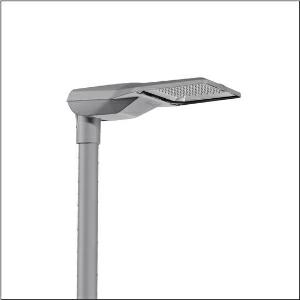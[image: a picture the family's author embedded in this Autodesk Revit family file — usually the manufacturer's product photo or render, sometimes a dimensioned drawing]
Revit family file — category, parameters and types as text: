
# Revit family: streetlight_sl_21_iq_midi___pc-r_5xe3g31g08mb_83c1
name_source: partatom
category: Lighting Fixtures
units: mm (PartAtom-declared; Revit-internal decimal feet)

## family parameters
Cut with Voids When Loaded = No
Host = Face
Light Source = No
Part Type = Normal
Room Calculation Point = No
Round Connector Dimension = Use Diameter
Shared = No

## types (1)
- --- (1 x LED, 18560 lm, 146.7 W, 3000K)
    Apparent Load = 147 VA
    CIE Flux Codes = 38 78 98 100 100
    Color Rendering = 70
    Color Temperature = 3000K
    Default Elevation = 1800 mm
    Description = Streetlight SL 21 iQ midi, mast luminaire, primary light control with lens, of PMMA, primary optical cover: cover, of toughened safety glass, transparent, light distribution: PC-R, light emission: direct distribution, primary light characteristic: asymmetric, right, installation type: post-top, side-entry, LED, High Power LED, rated luminous flux: 18.560lm, luminous efficacy: 127lm/W, light colour: 730, colour temperature: 3000K, control: Street-Remote, Auto-Match, Temp-Guard, Lumen-Switch, Night-Set, Smart-Wire, Light-Fading, Desk-Remote (wireless, voltage-free reading and setting of iQ features in the workshop via application-optimized NFC function/RFID function), optimised constant luminous flux control (CLO 2.0), presetting dimming linear, mains connection: 230..240V, AC, 50/60Hz, start of lifetime: 147W, end of service life: 161W, reduction: 62W, luminaire housing, of diecast aluminium, powder-coated, Siteco® metallic grey (DB 702S), corrosivity category C5 mid according to DIN EN ISO 12944, please order mast flange separately, inclination adjustable: 0°, 5°, 10°, 15°, sealing non-destructively replaceable, multi-level sealing system, length: 644mm, width: 335mm, height: 110mm, mast flange for spigot size: 42mm (side-entry): 5XC10008XM4, 60/48mm (side-entry/post-top): 5XC10108XM2, 76/60mm (side-entry/post-top): 5XC10108XM1, protection rating (complete): IP66, insulation class (complete): insulation class II (safety insulation), certification: CE, ENEC, ENEC+, VDE, impact resistance: IK09, permissible operating ambient temperature for outdoor applications: -40..+50°C, standard-compliant lighting for roads and squares, packaging unit: 1 piece

Light Distribution: PC-R
    Height = 111 mm
    Lamp = 1 x LED
    Lamp Light Flux = 18560 lm
    Lamp Power = 146.7 W
    Lamp count = 1
    Length = 644 mm
    Luminous efficacy = 127 lm/W
    Manufacturer = Siteco
    ModVariant = No
    Model = 5XE3G31G08MB
    Number of Poles = 1
    OnlyDefault = Yes
    Power Factor = 1
    Product Name = Streetlight SL 21 iQ midi | PC-R
    Product group = mast luminaire | pylon top
    ProductGroupID = 6100
    Protection Class = Protection class II
    Protection Degree = IP 66
    RLX_Detail_Level = 1
    RLX_Emergency_Light_Flux = 0 lm
    RLX_Emergency_Type = 0
    RLX_Emergency_Type_DB = No
    RlxData = <blob elided: 92933 chars, md5=54200fe3>
    Socket = socket
    Standby Power = 0 W
    System Light Flux = 18560 lm
    System Power = 147 W
    Type Comments = factory setting: luminous flux: 100 % | dim-lin: 254 | 753 mA
    Type Image = l_1004298.jpg
    URL = http://relux.com
    VarID = @adj_005143
    Voltage = 0 V
    Weight = 0.00 kg
    Width = 336 mm

## geometry (parser evidence)
native form markers: Blend x4, Sweep x11
no freeform markers — native parametric forms only
